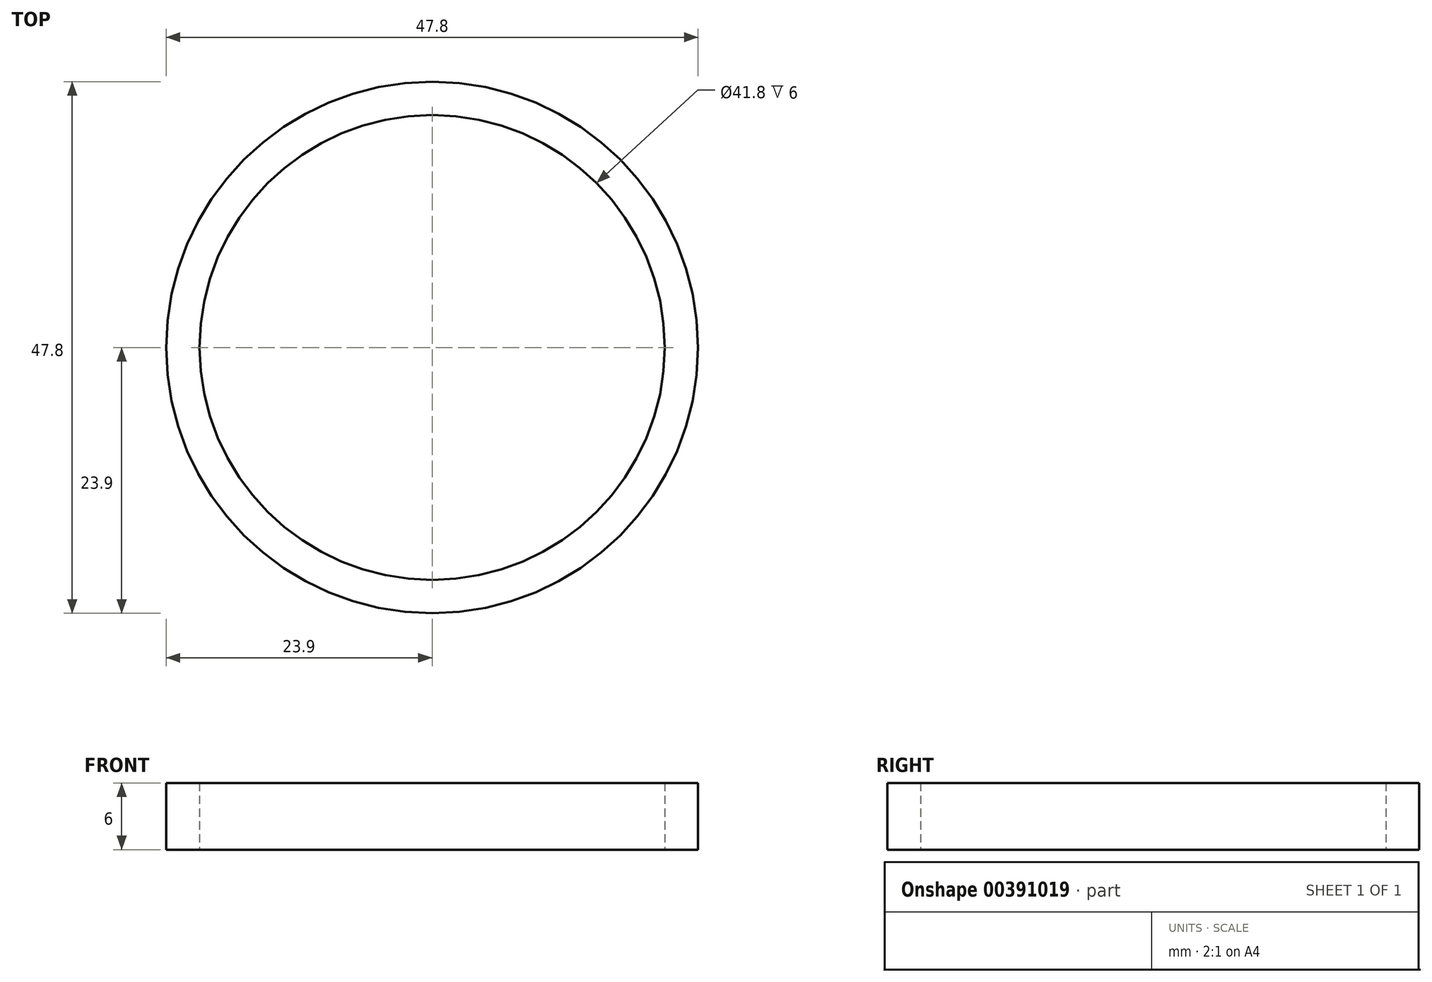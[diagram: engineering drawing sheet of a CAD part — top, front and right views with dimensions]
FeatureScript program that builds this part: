
annotation { "Feature Type Name" : "Feature", "Feature Type Description" : "" }
export const myFeature = defineFeature(function(context is Context, id is Id, definition is map)
    precondition{}
    {
        {
            var Q0;
            Q0=qCreatedBy(makeId("Top.planeOp"), FACE);
            var sketch = newSketch(context, id + "F0", { "sketchPlane" : qUnion([Q0])});
            skCircle(sketch, "E0", {"center": v(0, 0) * mm, "radius": 20.9 * mm});
            skCircle(sketch, "E1.0", {"center": v(0, 0) * mm, "radius": 23.9 * mm});
            skSolve(sketch);
        }
        {
            var Q0;
            Q0 = qSketchRegion(id + "F0", true);
            extrude(context, id + "F1", {"entities" : qUnion([Q0]), "domain" : OperationDomain.MODEL, "flatOperationType" : FlatOperationType.REMOVE, "depth" : 6 * mm, "offsetDistance" : 25 * mm});
        }
    });
